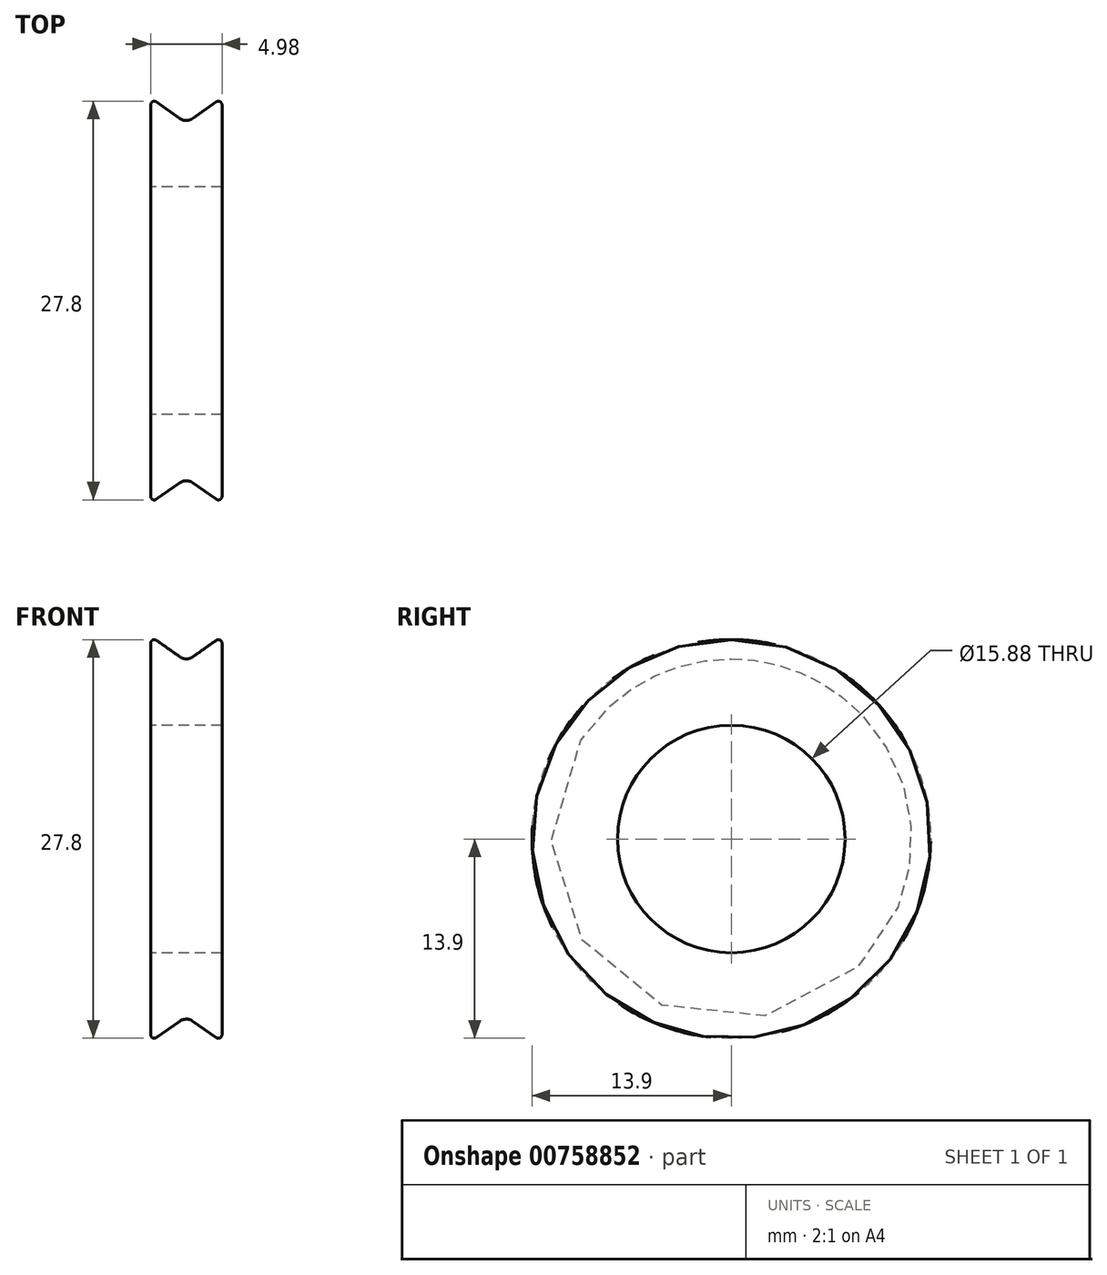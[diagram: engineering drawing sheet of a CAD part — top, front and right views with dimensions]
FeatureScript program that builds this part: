
annotation { "Feature Type Name" : "Feature", "Feature Type Description" : "" }
export const myFeature = defineFeature(function(context is Context, id is Id, definition is map)
    precondition{}
    {
        {
            var Q0;
            Q0=qCreatedBy(makeId("Front.planeOp"),FACE);
            var sketch = newSketch(context, id + "F0", { "sketchPlane" : qUnion([Q0])});
            skLineSegment(sketch, "E0", {"start": v(0, 0) * mm, "end": v(5.89, 0) * mm, "construction": true});
            skLineSegment(sketch, "E1", {"start": v(0.44, 12.7) * mm, "end": v(2.09, 13.86) * mm});
            skLineSegment(sketch, "E2", {"start": v(2.49, 7.94) * mm, "end": v(2.49, 13.65) * mm});
            skLineSegment(sketch, "E3", {"start": v(2.49, 7.94) * mm, "end": v(0, 7.94) * mm});
            skLineSegment(sketch, "E4", {"start": v(0, 7.94) * mm, "end": v(0, 12.4) * mm, "construction": true});
            skLineSegment(sketch, "E5.MirrorCS", {"start": v(-2.49, 7.94) * mm, "end": v(0, 7.94) * mm});
            skLineSegment(sketch, "E6.MirrorCS", {"start": v(-0.44, 12.7) * mm, "end": v(-2.09, 13.86) * mm});
            skLineSegment(sketch, "E7.MirrorCS", {"start": v(-2.49, 7.94) * mm, "end": v(-2.49, 13.65) * mm});
            skPoint(sketch, "E8.visualSharp", {"position": v(0, 12.4) * mm});
            skArc(sketch, "E8.filletArc", {"start": v(-0.44, 12.7) * mm, "mid": v(0, 12.56) * mm, "end": v(0.44, 12.7) * mm});
            skPoint(sketch, "E9.visualSharp", {"position": v(2.49, 14.14) * mm});
            skArc(sketch, "E9.filletArc", {"start": v(2.49, 13.65) * mm, "mid": v(2.35, 13.87) * mm, "end": v(2.09, 13.86) * mm});
            skPoint(sketch, "E10.visualSharp", {"position": v(-2.49, 14.14) * mm});
            skArc(sketch, "E10.filletArc", {"start": v(-2.09, 13.86) * mm, "mid": v(-2.35, 13.87) * mm, "end": v(-2.49, 13.65) * mm});
            skSolve(sketch);
        }
        {
            var Q0;
            Q0=makeQuery(id+"F0.imprint","IMPRINT",FACE,{"disambiguationData":[TD([[makeQuery(id+"F0.imprint","IMPRINT",EDGE,{"derivedFrom":sQuery(id+"F0.wireOp",EDGE,"E1")}),-1.0]])]});
            var Q1;
            Q1=sQuery(id+"F0.wireOp",EDGE,"E0");
            revolve(context, id + "F1", {"surfaceOperationType" : NewSurfaceOperationType.NEW, "entities" : qUnion([Q0]), "axis" : qUnion([Q1]), "revolveType" : RevolveType.FULL});
        }
    });
